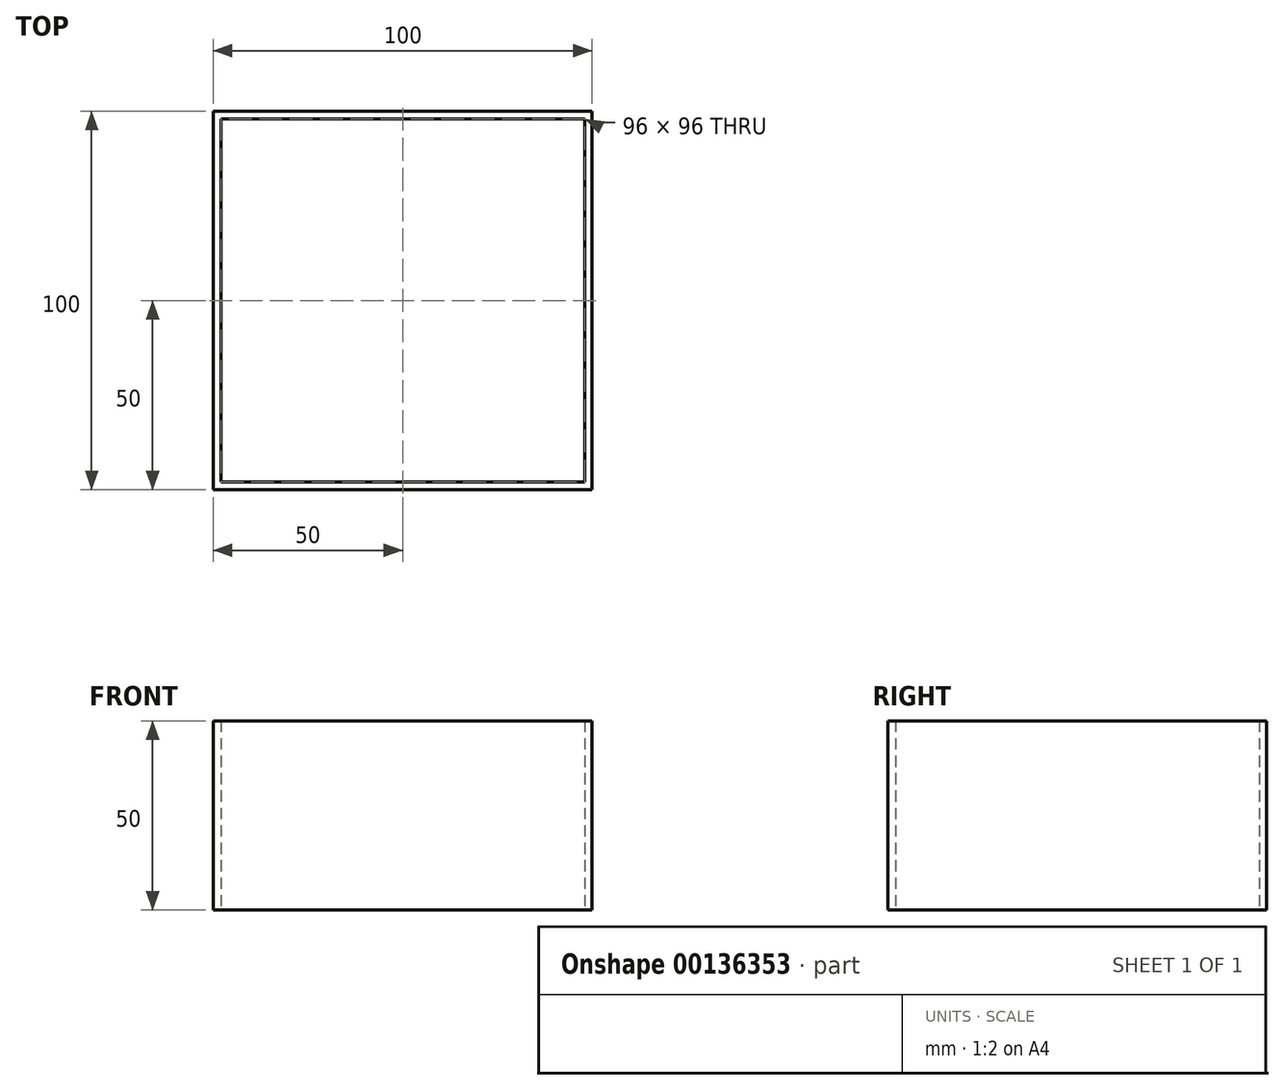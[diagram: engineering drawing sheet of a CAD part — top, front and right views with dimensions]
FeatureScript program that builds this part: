
annotation { "Feature Type Name" : "Feature", "Feature Type Description" : "" }
export const myFeature = defineFeature(function(context is Context, id is Id, definition is map)
    precondition{}
    {
        {
            var Q0;
            Q0=qCreatedBy(makeId("Top.planeOp"),FACE);
            var sketch = newSketch(context, id + "F0", { "sketchPlane" : qUnion([Q0])});
            skLineSegment(sketch, "E0.bottom", {"start": v(-50, 50) * mm, "end": v(50, 50) * mm});
            skLineSegment(sketch, "E0.top", {"start": v(-50, -50) * mm, "end": v(50, -50) * mm});
            skLineSegment(sketch, "E0.left", {"start": v(-50, 50) * mm, "end": v(-50, -50) * mm});
            skLineSegment(sketch, "E0.right", {"start": v(50, 50) * mm, "end": v(50, -50) * mm});
            skPoint(sketch, "E0.middle", {"position": v(0, 0) * mm});
            skLineSegment(sketch, "E1.bottom", {"start": v(-48, 48) * mm, "end": v(48, 48) * mm});
            skLineSegment(sketch, "E1.top", {"start": v(-48, -48) * mm, "end": v(48, -48) * mm});
            skLineSegment(sketch, "E1.left", {"start": v(-48, 48) * mm, "end": v(-48, -48) * mm});
            skLineSegment(sketch, "E1.right", {"start": v(48, 48) * mm, "end": v(48, -48) * mm});
            skSolve(sketch);
        }
        {
            var Q0;
            Q0=makeQuery(id+"F0.imprint","IMPRINT",FACE,{"disambiguationData":[TD([[makeQuery(id+"F0.imprint","IMPRINT",EDGE,{"derivedFrom":sQuery(id+"F0.wireOp",EDGE,"E0.bottom")}),-1.0]])]});
            extrude(context, id + "F1", {"entities" : qUnion([Q0]), "depth" : 50 * mm});
        }
    });
